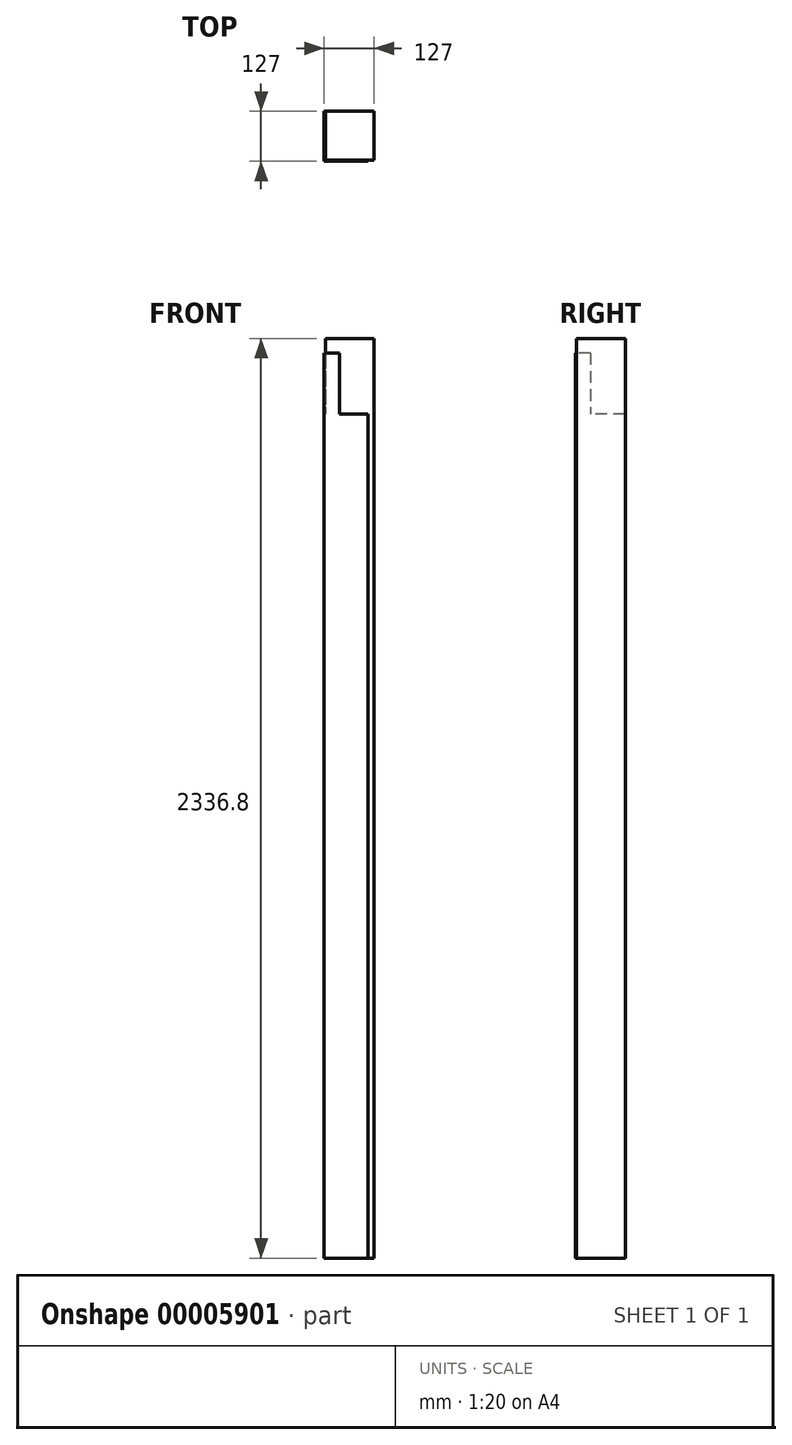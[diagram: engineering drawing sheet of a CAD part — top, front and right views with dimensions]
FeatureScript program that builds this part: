
annotation { "Feature Type Name" : "Feature", "Feature Type Description" : "" }
export const myFeature = defineFeature(function(context is Context, id is Id, definition is map)
    precondition{}
    {
        {
            var Q0;
            Q0=qCreatedBy(makeId("Top.planeOp"),FACE);
            var sketch = newSketch(context, id + "F0", { "sketchPlane" : qUnion([Q0])});
            skLineSegment(sketch, "E0.bottom", {"start": v(0, 0) * mm, "end": v(127, 0) * mm});
            skLineSegment(sketch, "E0.top", {"start": v(0, 127) * mm, "end": v(127, 127) * mm});
            skLineSegment(sketch, "E0.left", {"start": v(0, 0) * mm, "end": v(0, 127) * mm});
            skLineSegment(sketch, "E0.right", {"start": v(127, 0) * mm, "end": v(127, 127) * mm});
            skSolve(sketch);
        }
        {
            var Q0;
            Q0=makeQuery(id+"F0.imprint","IMPRINT",FACE,{"disambiguationData":[TD([[makeQuery(id+"F0.imprint","IMPRINT",EDGE,{"derivedFrom":sQuery(id+"F0.wireOp",EDGE,"E0.bottom")}),1.0]])]});
            extrude(context, id + "F1", {"entities" : qUnion([Q0]), "depth" : 2336.8 * mm});
        }
        {
            var Q0;
            Q0=makeQuery(id+"F1.opExtrude","SWEPT_FACE",FACE,{"disambiguationData":[OSD([sQuery(id+"F0.wireOp",EDGE,"E0.bottom")])]});
            var sketch = newSketch(context, id + "F2", { "sketchPlane" : qUnion([Q0])});
            skLineSegment(sketch, "E1.bottom", {"start": v(127, 2336.8) * mm, "end": v(0, 2336.8) * mm});
            skLineSegment(sketch, "E1.top", {"start": v(38.9, 2300.29) * mm, "end": v(0, 2300.29) * mm});
            skLineSegment(sketch, "E1.left", {"start": v(127, 2336.8) * mm, "end": v(127, 2300.29) * mm});
            skLineSegment(sketch, "E1.right", {"start": v(0, 2336.8) * mm, "end": v(0, 2300.29) * mm});
            skLineSegment(sketch, "E2.top", {"start": v(111.12, 2144.71) * mm, "end": v(38.9, 2144.71) * mm});
            skLineSegment(sketch, "E2.left", {"start": v(127, 2300.29) * mm, "end": v(127, 2144.71) * mm});
            skLineSegment(sketch, "E2.right", {"start": v(38.9, 2300.29) * mm, "end": v(38.9, 2144.71) * mm});
            skLineSegment(sketch, "E3.top", {"start": v(127, 0) * mm, "end": v(111.13, 0) * mm});
            skLineSegment(sketch, "E3.left", {"start": v(127, 2144.71) * mm, "end": v(127, 0) * mm});
            skLineSegment(sketch, "E3.right", {"start": v(111.13, 2144.71) * mm, "end": v(111.13, 0) * mm});
            skLineSegment(sketch, "E4", {"start": v(63.5, 2336.8) * mm, "end": v(63.5, 2144.71) * mm, "construction": true});
            skLineSegment(sketch, "E5", {"start": v(0, 2249.22) * mm, "end": v(38.9, 2249.22) * mm, "construction": true});
            skLineSegment(sketch, "E6", {"start": v(127, 2099.04) * mm, "end": v(111.13, 2099.04) * mm, "construction": true});
            skSolve(sketch);
        }
        {
            var Q0;
            Q0=makeQuery(id+"F2.imprint","IMPRINT",FACE,{"disambiguationData":[TD([[makeQuery(id+"F2.imprint","IMPRINT",EDGE,{"derivedFrom":sQuery(id+"F2.wireOp",EDGE,"E1.bottom")}),-1.0]])]});
            extrude(context, id + "F3", {"entities" : qUnion([Q0]), "operationType" : NewBodyOperationType.REMOVE, "oppositeDirection" : true, "depth" : 3.17 * mm});
        }
        {
            var Q0;
            Q0=makeQuery(id+"F1.opExtrude","SWEPT_FACE",FACE,{"disambiguationData":[OSD([sQuery(id+"F0.wireOp",EDGE,"E0.left")])]});
            var sketch = newSketch(context, id + "F4", { "sketchPlane" : qUnion([Q0])});
            skLineSegment(sketch, "E7.top", {"start": v(-3.18, 2300.29) * mm, "end": v(0, 2300.29) * mm});
            skLineSegment(sketch, "E7.left", {"start": v(-3.18, 2336.8) * mm, "end": v(-3.18, 2300.29) * mm});
            skLineSegment(sketch, "E8.top", {"start": v(-127, 2336.8) * mm, "end": v(-3.17, 2336.8) * mm});
            skLineSegment(sketch, "E8.left", {"start": v(-127, 2300.29) * mm, "end": v(-127, 2336.8) * mm});
            skLineSegment(sketch, "E9.top", {"start": v(-127, 2144.71) * mm, "end": v(-38.9, 2144.71) * mm});
            skLineSegment(sketch, "E9.left", {"start": v(-127, 2300.29) * mm, "end": v(-127, 2144.71) * mm});
            skLineSegment(sketch, "E9.right", {"start": v(-38.9, 2300.29) * mm, "end": v(-38.9, 2144.71) * mm});
            skLineSegment(sketch, "E10", {"start": v(0, 2259.12) * mm, "end": v(-38.9, 2259.12) * mm, "construction": true});
            skLineSegment(sketch, "E11", {"start": v(-86.87, 2336.8) * mm, "end": v(-86.87, 2144.71) * mm, "construction": true});
            skLineSegment(sketch, "E12.trimOffspring", {"start": v(-38.9, 2300.29) * mm, "end": v(0, 2300.29) * mm});
            skLineSegment(sketch, "E13.bottom", {"start": v(-127, 2144.71) * mm, "end": v(-111.12, 2144.71) * mm});
            skLineSegment(sketch, "E13.top", {"start": v(-127, 0) * mm, "end": v(-111.12, 0) * mm});
            skLineSegment(sketch, "E13.left", {"start": v(-127, 2144.71) * mm, "end": v(-127, 0) * mm});
            skLineSegment(sketch, "E13.right", {"start": v(-111.12, 2144.71) * mm, "end": v(-111.12, 0) * mm});
            skSolve(sketch);
        }
        {
            var Q0;
            {var subQ0=makeQuery(id+"F4.imprint","IMPRINT",EDGE,{"derivedFrom":sQuery(id+"F4.wireOp",EDGE,"E13.bottom")});var subQ3=sQuery(id+"F4.wireOp",EDGE,"E7.left");Q0=qUnion([makeQuery(id+"F4.imprint","IMPRINT",FACE,{"disambiguationData":[TD([[makeQuery(id+"F4.imprint","IMPRINT",EDGE,{"derivedFrom":subQ3}),-1.0]])]}),makeQuery(id+"F4.imprint","IMPRINT",FACE,{"disambiguationData":[TD([[subQ0,-1.0]])]})]);}
            extrude(context, id + "F5", {"entities" : qUnion([Q0]), "operationType" : NewBodyOperationType.REMOVE, "oppositeDirection" : true, "depth" : 3.17 * mm});
        }
    });
